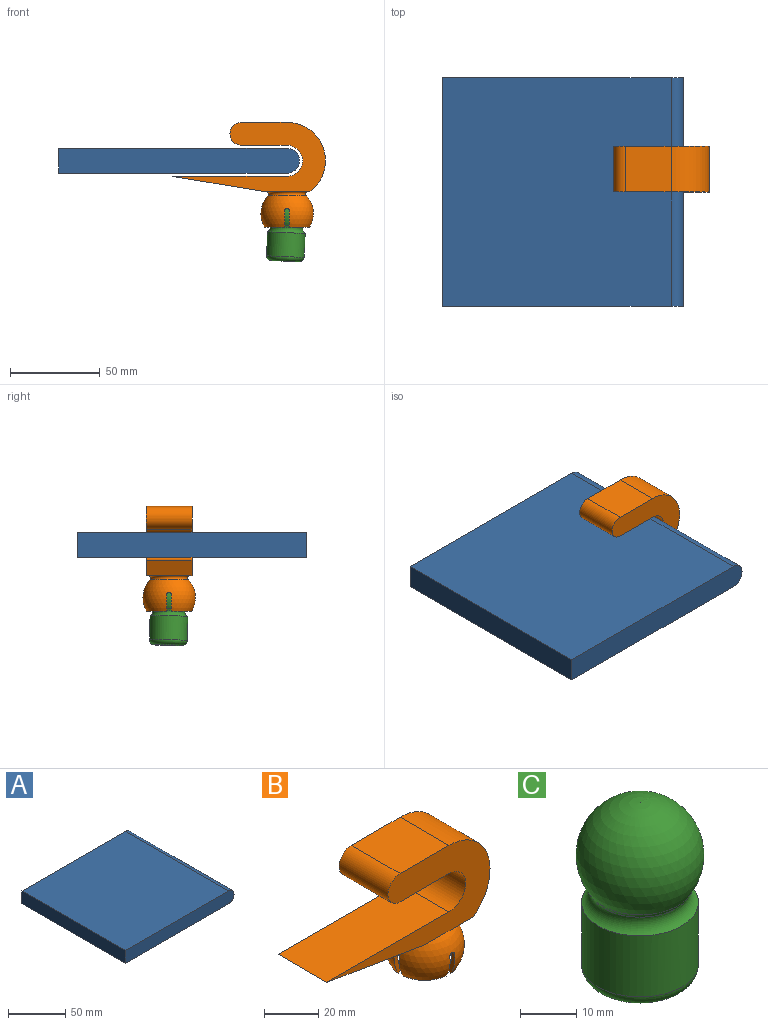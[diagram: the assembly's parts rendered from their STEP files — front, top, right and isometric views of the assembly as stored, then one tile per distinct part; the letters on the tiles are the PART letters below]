
ASSEMBLY  parts=3 mates=2
PART A: 6 faces, bbox 133.9x127x13.7 mm
  f0: cylinder r=6.85mm len=127mm, axis (0,1,0), area 2733mm2, adj f1,f3,f4,f5
  f1: plane 127x127mm, normal (0,0,1), area 16129mm2, adj f0,f2,f4,f5
  f2: plane 127x13.7mm, normal (-1,0,0), area 1739.9mm2, adj f1,f3,f4,f5
  f3: plane 127x127mm, normal (0,0,-1), area 16129mm2, adj f0,f2,f4,f5
  f4: plane 133.85x13.7mm, normal (0,-1,0), area 1813.6mm2, adj f0,f1,f2,f3
  f5: plane 133.85x13.7mm, normal (0,1,0), area 1813.6mm2, adj f0,f1,f2,f3
PART B: 34 faces, bbox 84.8x29.2x58.3 mm
  f0: cone r=12.64mm half-angle=65.1deg, axis (0,0,-1), area 30.1mm2, adj f2,f4,f19,f20
  f1: plane 9.48x3.88mm, normal (0,1,0), area 18.1mm2, adj f19,f20,f22,f26
  f2: plane 9.48x3.88mm, normal (0,-1,0), area 18.1mm2, adj f0,f19,f20,f25
  f3: cone r=12.64mm half-angle=65.1deg, axis (0,0,-1), area 30.1mm2, adj f5,f7,f19,f20
  f4: plane 9.48x3.88mm, normal (-1,0,0), area 18.1mm2, adj f0,f19,f20,f28
  f5: plane 9.48x3.88mm, normal (1,0,0), area 18.1mm2, adj f3,f19,f20,f27
  f6: cone r=12.64mm half-angle=65.1deg, axis (0,0,-1), area 30.1mm2, adj f8,f19,f20,f23
  f7: plane 9.48x3.88mm, normal (0,-1,0), area 18.1mm2, adj f3,f19,f20,f30
  f8: plane 9.48x3.88mm, normal (0,1,0), area 18.1mm2, adj f6,f19,f20,f29
  f9: plane 25.4x25.4mm, normal (0,0,-1), area 235.4mm2, adj f10,f16,f17,f18,f33
  f10: cylinder r=21.33mm len=38.46mm, axis (0,1,0), area 1356.4mm2, adj f9,f11,f17,f18
  f11: plane 25.4x25.4mm, normal (0,0,1), area 645.2mm2, adj f10,f12,f17,f18
  f12: cylinder r=6.35mm len=25.4mm, axis (0,1,0), area 506.7mm2, adj f11,f13,f17,f18
  f13: plane 25.4x25.4mm, normal (0,0,-1), area 645.2mm2, adj f12,f14,f17,f18
  f14: cylinder r=8.63mm len=25.4mm, axis (0,1,0), area 688.5mm2, adj f13,f15,f17,f18
  f15: plane 63.5x25.4mm, normal (0,0,1), area 1612.9mm2, adj f14,f16,f17,f18
  f16: plane 50.8x25.4mm, normal (-0.17,0,-0.99), area 1308.3mm2, adj f9,f15,f17,f18
  f17: plane 84.83x38.46mm, normal (0,-1,0), area 1271.3mm2, adj f9,f10,f11,f12,f13,f14,f15,f16
  f18: plane 84.83x38.46mm, normal (0,1,0), area 1271.3mm2, adj f9,f10,f11,f12,f13,f14,f15,f16
  f19: sphere r=12.7mm, area 1417.7mm2, adj f0,f1,f2,f3,f4,f5,f6,f7
  f20: sphere r=14.61mm, area 1514mm2, adj f0,f1,f2,f3,f4,f5,f6,f7
  f21: plane 6.35x6.35mm, normal (0,0,-1), area 31.7mm2, adj f19
  f22: cone r=12.64mm half-angle=65.1deg, axis (0,0,-1), area 30.1mm2, adj f1,f19,f20,f24
  f23: plane 9.48x3.88mm, normal (1,0,0), area 18.1mm2, adj f6,f19,f20,f32
  f24: plane 9.48x3.88mm, normal (-1,0,0), area 18.1mm2, adj f19,f20,f22,f31
  f25: cylinder r=1.27mm len=2.13mm, axis (-1,0,0), area 3.9mm2, adj f2,f19,f20,f26
  f26: cylinder r=1.27mm len=2.13mm, axis (1,0,0), area 3.9mm2, adj f1,f19,f20,f25
  f27: cylinder r=1.27mm len=2.13mm, axis (0,-1,0), area 3.9mm2, adj f5,f19,f20,f28
  f28: cylinder r=1.27mm len=2.13mm, axis (0,1,0), area 3.9mm2, adj f4,f19,f20,f27
  f29: cylinder r=1.27mm len=2.13mm, axis (1,0,0), area 3.9mm2, adj f8,f19,f20,f30
  f30: cylinder r=1.27mm len=2.13mm, axis (-1,0,0), area 3.9mm2, adj f7,f19,f20,f29
  f31: cylinder r=1.27mm len=2.13mm, axis (0,1,0), area 3.9mm2, adj f19,f20,f24,f32
  f32: cylinder r=1.27mm len=2.13mm, axis (0,-1,0), area 3.9mm2, adj f19,f20,f23,f31
  f33: torus R=11.42mm, axis (0,0,1), area 196mm2, adj f9,f20
PART C: 8 faces, bbox 24.8x24.8x37.7 mm
  f0: sphere r=11.43mm, area 1283.5mm2, adj f5
  f1: plane 8.2x8.2mm, normal (0,0,-1), area 52.8mm2, adj f2
  f2: cylinder r=4.1mm len=9.53mm, axis (0,0,-1), area 245.4mm2, adj f1,f3
  f3: plane 15.82x15.82mm, normal (0,0,-1), area 143.8mm2, adj f2,f7
  f4: cylinder r=10.45mm len=20.9mm, axis (0,0,-1), area 875.6mm2, adj f6,f7
  f5: torus R=12.06mm, axis (0,0,1), area 51mm2, adj f0,f6
  f6: torus R=11.46mm, axis (0,0,-1), area 221.2mm2, adj f4,f5
  f7: torus R=7.91mm, axis (0,0,1), area 238.8mm2, adj f3,f4
PLACE A t=(0,-12.7,0)mm fixed
PLACE B at identity
PLACE C rot(axis=(0.36,0.91,0.22),2.5deg) t=(1.19,-0.47,-0.03)mm
MATE fastened B.f14 <-> A.f0  axis (0,-1,0) through (0,-12.7,0)mm
MATE ball B.f33 <-> C.f2  axis (0,0,1) through (0,0,-29.43)mm
